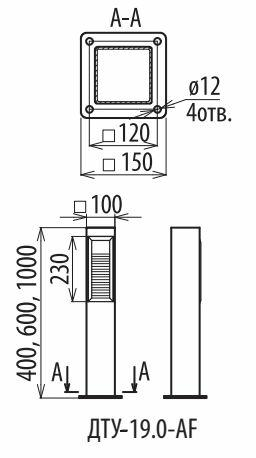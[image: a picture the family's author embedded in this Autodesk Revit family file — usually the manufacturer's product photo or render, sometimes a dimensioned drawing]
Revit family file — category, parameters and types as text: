
# Revit family: svetilnik_alfresco_solo
name_source: partatom
category: Осветительные приборы
revit_build: Autodesk Revit 2016 (Build: 20150506_1715(x64)
units: mm (PartAtom-declared; Revit-internal decimal feet)

## family parameters
Всегда вертикально = Да
Источник света = Да
На основе рабочей плоскости = Нет
Общий = Нет
При загрузке вырезать с полостями = Нет
Размер круглого соединителя = Использовать диаметр
Тип детали = Нормальный
Точка расчета площади = Нет

## types (4) — shared parameters
ADSK_Единица измерения = шт.
ADSK_Завод-изготовитель = ALFRESCO
ADSK_Количество фаз = 2
ADSK_Количество фаз числовое = 2
ADSK_Коэффициент мощности = 0.98
ADSK_Модель = ДТУ-22-AF Соло
ADSK_Напряжение = 220 В
ADSK_Ток = 0 А
ADSK_Энергоэффективность = 110 лм/Вт
IP Class = IP 66
URL = http://www.allfresco.ru
Блок аварийного питания = Нет
Видимая форма излучения при визуализации = Нет
Высота крышки = 40 мм
Изготовитель = ALFRESCO
Излучение по диаметру окружности = 100 мм
Класс защиты = 1
Класс пожароопасности = F (светильники предназначены для установки непосредственно на поверхность из нормально воспламеняемых материалов)
Климатическая зона = У1
Корпус светильника = Сталь крашенная чёрная
Материал рассеивателя = PC
Область использования = ландшафт, коттедж. Посёлки,микрорайоны
Плафон = PC
Радиус  корпуса светильника = 54 мм
Радиус фланца = 95 мм
Светофильтр = 16777215
Смещение цветовой температуры при затухании лампы = <Нет>
Температура эксплуатации = -35 +40
Тип ИС = LED-светодиоды
Тип КСС = Круглосимметричная
Тип ПРА = -
Тип продукции = LED-светильник
Угол наклона = 90.00°
Цветовая температура = 2700-6500
Ширина корпуса = 108 мм

## per-type parameters (varying)
| type | ADSK_Артикул | ADSK_Масса | ADSK_Наименование | ADSK_Номинальная мощность | ADSK_Полная мощность | ADSK_Размер_Высота | Высота плафона | Полная установленная мощность | Файл фотометрической сетки |
| Соло-1,0 | ДТУ2214 | 9 | Светодиодный светильник Соло ДТУ-22-AF-12Вт-1,0-IP66 | 12 Вт | 12 В·А | 1000 мм | 460 мм | 12 В·А | solo12W 1m.ies |
| Соло-1,5 (1) | ДТУ2216 | 10.1 | Светодиодный светильник Соло ДТУ-22-AF-12Вт-1,5-IP66 | 12 Вт | 12 В·А | 1500 мм | 656 мм | 12 В·А | solo12W 1,5m.ies |
| Соло-1,5 (2) | ДТУ2215 | 10.2 | Светодиодный светильник Соло ДТУ-22-AF-25Вт-1,5-IP66 | 25 Вт | 26 В·А | 1500 мм | 656 мм | 26 В·А | solo25W 1,5m.ies |
| Соло-2 | ДТУ2212 | 11.2 | Светодиодный светильник Соло ДТУ-22-AF-25Вт-2,0-IP66 | 25 Вт | 26 В·А | 2000 мм | 1156 мм | 26 В·А | solo25W 2m.ies |

## geometry (parser evidence)
native form markers: Blend x2
no freeform markers — native parametric forms only
